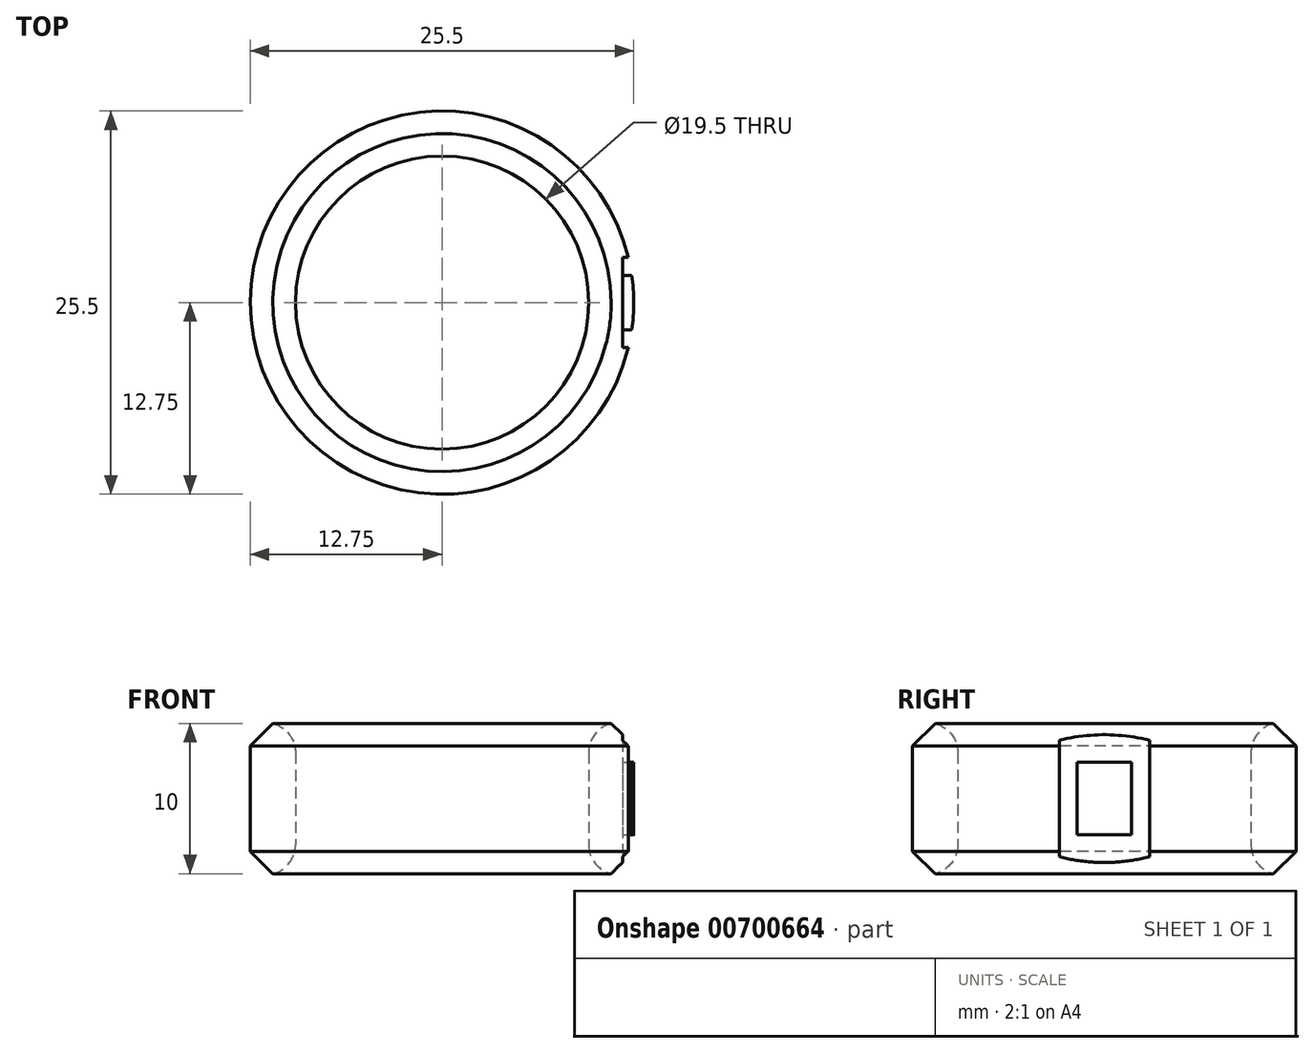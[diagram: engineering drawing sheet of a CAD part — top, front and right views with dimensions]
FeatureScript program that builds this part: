
annotation { "Feature Type Name" : "Feature", "Feature Type Description" : "" }
export const myFeature = defineFeature(function(context is Context, id is Id, definition is map)
    precondition{}
    {
        {
            var Q0;
            Q0=qCreatedBy(makeId("Top.planeOp"),FACE);
            var sketch = newSketch(context, id + "F0", { "sketchPlane" : qUnion([Q0])});
            skCircle(sketch, "E0", {"center": v(0, 0) * mm, "radius": 9.75 * mm});
            skCircle(sketch, "E1", {"center": v(0, 0) * mm, "radius": 12.75 * mm});
            skSolve(sketch);
        }
        {
            var Q0;
            Q0=makeQuery(id+"F0.imprint","IMPRINT",FACE,{"disambiguationData":[TD([[makeQuery(id+"F0.imprint","IMPRINT",EDGE,{"derivedFrom":sQuery(id+"F0.wireOp",EDGE,"E0")}),-1.0]])]});
            extrude(context, id + "F1", {"entities" : qUnion([Q0]), "depth" : 10 * mm, "offsetDistance" : 25 * mm});
        }
        {
            var Q0;
            Q0=makeQuery(id+"F1.opExtrude","CAP_EDGE",EDGE,{"disambiguationData":[OSD([sQuery(id+"F0.wireOp",EDGE,"E1")])],"isStart":false});
            var Q1;
            Q1=makeQuery(id+"F1.opExtrude","CAP_EDGE",EDGE,{"disambiguationData":[OSD([sQuery(id+"F0.wireOp",EDGE,"E1")])],"isStart":true});
            chamfer(context, id + "F2", {"entities" : qUnion([Q0, Q1]), "width" : 1.5 * mm, "tangentPropagation" : true});
        }
        {
            var Q0;
            Q0=qCreatedBy(makeId("Right.planeOp"),FACE);
            cPlane(context, id + "F3", {"entities" : qUnion([Q0]), "cplaneType" : CPlaneType.OFFSET, "offset" : 14 * mm, "width" : 150 * mm, "height" : 150 * mm});
        }
        {
            var Q0;
            Q0=qCreatedBy(id+"F3.planeOp",FACE);
            var sketch = newSketch(context, id + "F4", { "sketchPlane" : qUnion([Q0])});
            skLineSegment(sketch, "E2.bottom", {"start": v(3, 10) * mm, "end": v(-3, 10) * mm});
            skLineSegment(sketch, "E2.top", {"start": v(3, 0) * mm, "end": v(-3, 0) * mm});
            skLineSegment(sketch, "E2.left", {"start": v(3, 10) * mm, "end": v(3, 0) * mm});
            skLineSegment(sketch, "E2.right", {"start": v(-3, 10) * mm, "end": v(-3, 0) * mm});
            skPoint(sketch, "E2.middle", {"position": v(0, 5) * mm});
            skLineSegment(sketch, "E3.bottom", {"start": v(1.8, 7.42) * mm, "end": v(-1.8, 7.42) * mm});
            skLineSegment(sketch, "E3.top", {"start": v(1.8, 2.59) * mm, "end": v(-1.8, 2.59) * mm});
            skLineSegment(sketch, "E3.left", {"start": v(1.8, 7.42) * mm, "end": v(1.8, 2.59) * mm});
            skLineSegment(sketch, "E3.right", {"start": v(-1.8, 7.42) * mm, "end": v(-1.8, 2.59) * mm});
            skSolve(sketch);
        }
        {
            var Q0;
            Q0=makeQuery(id+"F4.imprint","IMPRINT",FACE,{"disambiguationData":[TD([[makeQuery(id+"F4.imprint","IMPRINT",EDGE,{"derivedFrom":sQuery(id+"F4.wireOp",EDGE,"E2.bottom")}),1.0]])]});
            extrude(context, id + "F5", {"entities" : qUnion([Q0]), "operationType" : NewBodyOperationType.REMOVE, "depth" : -2 * mm, "offsetDistance" : 25 * mm});
        }
        {
            var Q0;
            Q0=makeQuery(id+"F1.opExtrude","CAP_EDGE",EDGE,{"disambiguationData":[OSD([sQuery(id+"F0.wireOp",EDGE,"E0")])],"isStart":false});
            var Q1;
            Q1=makeQuery(id+"F1.opExtrude","CAP_EDGE",EDGE,{"disambiguationData":[OSD([sQuery(id+"F0.wireOp",EDGE,"E0")])],"isStart":true});
            fillet(context, id + "F6", {"entities" : qUnion([Q0, Q1]), "radius" : 2 * mm, "tangentPropagation" : true, "allowEdgeOverflow" : false});
        }
    });
